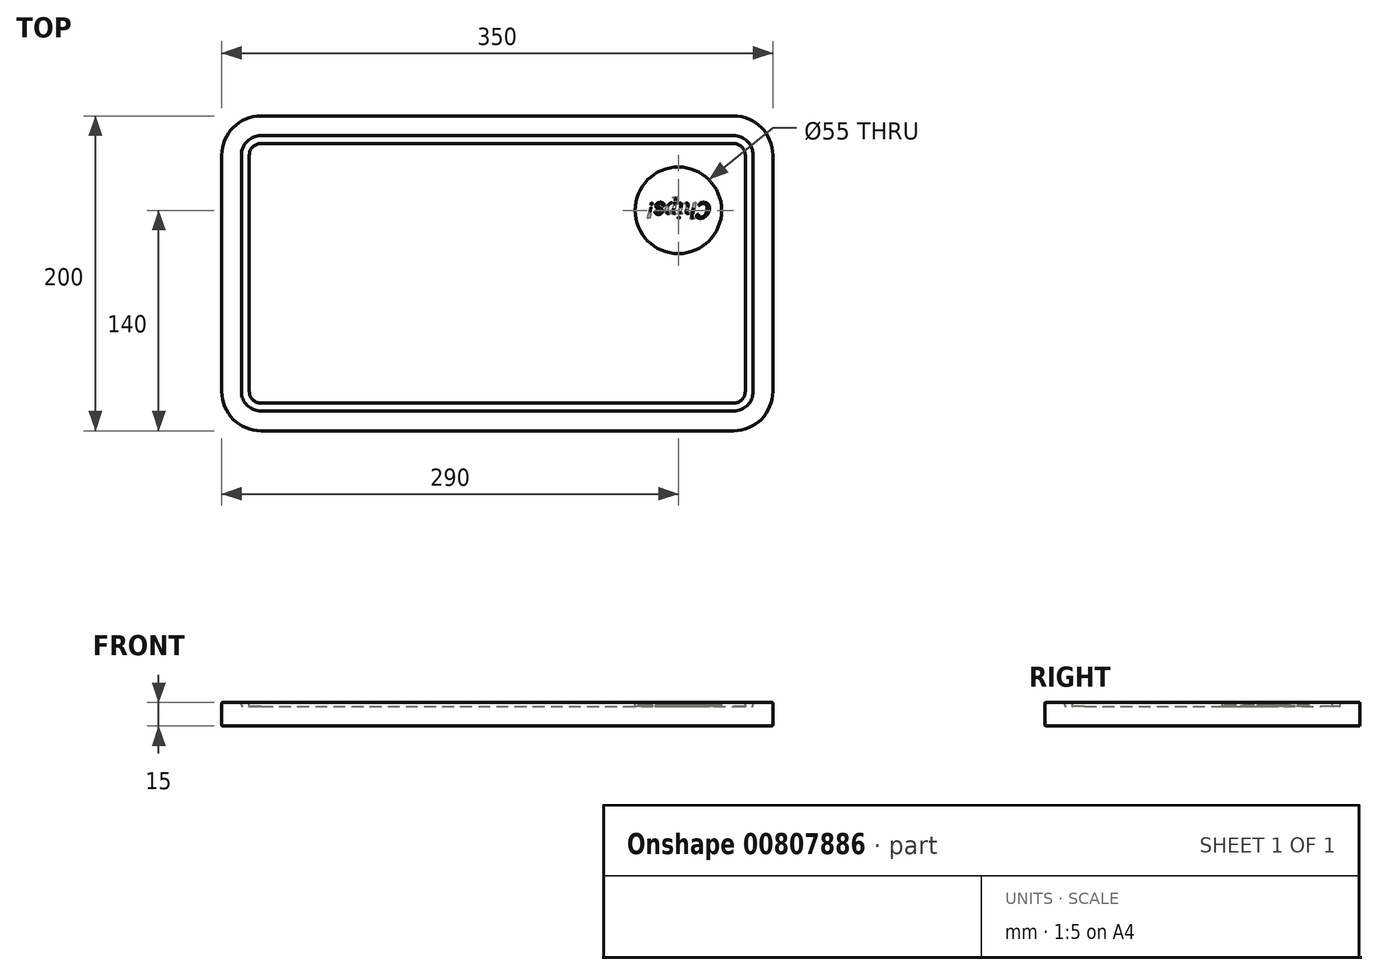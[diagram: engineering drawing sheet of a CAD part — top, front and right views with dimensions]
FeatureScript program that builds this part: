
annotation { "Feature Type Name" : "Feature", "Feature Type Description" : "" }
export const myFeature = defineFeature(function(context is Context, id is Id, definition is map)
    precondition{}
    {
        {
            assignVariable(context, id + "F0", {"name" : "BrdThk", "anyValue" : 15 * mm});
        }
        {
            assignVariable(context, id + "F1", {"name" : "CrnRad", "anyValue" : 25 * mm});
        }
        {
            assignVariable(context, id + "F2", {"name" : "GrvDpth", "anyValue" : 2.5 * mm});
        }
        {
            var Q0;
            Q0=qCreatedBy(makeId("Top.planeOp"),FACE);
            cPlane(context, id + "F3", {"entities" : qUnion([Q0]), "cplaneType" : CPlaneType.OFFSET, "offset" : getVariable(context, 'BrdThk'), "width" : 150 * mm, "height" : 150 * mm});
        }
        {
            var Q0;
            Q0=qCreatedBy(id+"F3.planeOp",FACE);
            cPlane(context, id + "F4", {"entities" : qUnion([Q0]), "cplaneType" : CPlaneType.OFFSET, "offset" : getVariable(context, 'GrvDpth'), "oppositeDirection" : true, "width" : 150 * mm, "height" : 150 * mm});
        }
        {
            var Q0;
            Q0=qCreatedBy(makeId("Top.planeOp"),FACE);
            var sketch = newSketch(context, id + "F5", { "sketchPlane" : qUnion([Q0])});
            skLineSegment(sketch, "E0.bottom", {"start": v(-350, 0) * mm, "end": v(0, 0) * mm});
            skLineSegment(sketch, "E0.top", {"start": v(-350, -200) * mm, "end": v(0, -200) * mm});
            skLineSegment(sketch, "E0.left", {"start": v(-350, 0) * mm, "end": v(-350, -200) * mm});
            skLineSegment(sketch, "E0.right", {"start": v(0, 0) * mm, "end": v(0, -200) * mm});
            skLineSegment(sketch, "E1", {"start": v(-76.31, 0) * mm, "end": v(-267.45, 0) * mm, "construction": true});
            skLineSegment(sketch, "E2", {"start": v(0, 111.25) * mm, "end": v(0, -79.9) * mm, "construction": true});
            skSolve(sketch);
        }
        {
            var Q0;
            Q0=makeQuery(id+"F5.imprint","IMPRINT",FACE,{"disambiguationData":[TD([[makeQuery(id+"F5.imprint","IMPRINT",EDGE,{"derivedFrom":sQuery(id+"F5.wireOp",EDGE,"E0.bottom")}),-1.0]])]});
            var Q1;
            Q1=qCreatedBy(id+"F3.planeOp",FACE);
            extrude(context, id + "F6", {"entities" : qUnion([Q0]), "endBound" : BoundingType.UP_TO_SURFACE, "depth" : 15 * mm, "endBoundEntityFace" : qUnion([Q1]), "offsetDistance" : 25 * mm});
        }
        {
            var Q0;
            Q0=makeQuery(id+"F6.opExtrude","SWEPT_EDGE",EDGE,{"disambiguationData":[OSD([sQuery(id+"F5.wireOp",EDGE,"E0.top"),sQuery(id+"F5.wireOp",EDGE,"E0.left")])]});
            var Q1;
            Q1=makeQuery(id+"F6.opExtrude","SWEPT_EDGE",EDGE,{"disambiguationData":[OSD([sQuery(id+"F5.wireOp",EDGE,"E0.bottom"),sQuery(id+"F5.wireOp",EDGE,"E0.left")])]});
            var Q2;
            Q2=makeQuery(id+"F6.opExtrude","SWEPT_EDGE",EDGE,{"disambiguationData":[OSD([sQuery(id+"F5.wireOp",EDGE,"E0.bottom"),sQuery(id+"F5.wireOp",EDGE,"E0.right")])]});
            var Q3;
            Q3=makeQuery(id+"F6.opExtrude","SWEPT_EDGE",EDGE,{"disambiguationData":[OSD([sQuery(id+"F5.wireOp",EDGE,"E0.top"),sQuery(id+"F5.wireOp",EDGE,"E0.right")])]});
            fillet(context, id + "F7", {"entities" : qUnion([Q0, Q1, Q2, Q3]), "radius" : getVariable(context, 'CrnRad'), "tangentPropagation" : true, "allowEdgeOverflow" : false});
        }
        {
            var Q0;
            Q0=qCreatedBy(id+"F3.planeOp",FACE);
            var sketch = newSketch(context, id + "F8", { "sketchPlane" : qUnion([Q0])});
            skLineSegment(sketch, "E3.0.0", {"start": v(-350, -25) * mm, "end": v(-350, -175) * mm, "construction": true});
            skArc(sketch, "E3.0.1", {"start": v(-350, -175) * mm, "mid": v(-342.68, -192.68) * mm, "end": v(-325, -200) * mm, "construction": true});
            skLineSegment(sketch, "E3.0.2", {"start": v(-325, -200) * mm, "end": v(-25, -200) * mm, "construction": true});
            skArc(sketch, "E3.0.3", {"start": v(-25, -200) * mm, "mid": v(-7.32, -192.68) * mm, "end": v(0, -175) * mm, "construction": true});
            skLineSegment(sketch, "E3.0.4", {"start": v(0, -175) * mm, "end": v(0, -25) * mm, "construction": true});
            skArc(sketch, "E3.0.5", {"start": v(0, -25) * mm, "mid": v(-7.32, -7.32) * mm, "end": v(-25, 0) * mm, "construction": true});
            skLineSegment(sketch, "E3.0.6", {"start": v(-25, 0) * mm, "end": v(-325, 0) * mm, "construction": true});
            skArc(sketch, "E3.0.7", {"start": v(-325, 0) * mm, "mid": v(-342.68, -7.32) * mm, "end": v(-350, -25) * mm, "construction": true});
            skArc(sketch, "E4.0", {"start": v(-325, -12.5) * mm, "mid": v(-333.84, -16.16) * mm, "end": v(-337.5, -25) * mm});
            skLineSegment(sketch, "E4.1", {"start": v(-25, -12.5) * mm, "end": v(-325, -12.5) * mm});
            skLineSegment(sketch, "E4.2", {"start": v(-337.5, -25) * mm, "end": v(-337.5, -175) * mm});
            skArc(sketch, "E4.3", {"start": v(-12.5, -25) * mm, "mid": v(-16.16, -16.16) * mm, "end": v(-25, -12.5) * mm});
            skArc(sketch, "E4.4", {"start": v(-337.5, -175) * mm, "mid": v(-333.84, -183.84) * mm, "end": v(-325, -187.5) * mm});
            skLineSegment(sketch, "E4.5", {"start": v(-325, -187.5) * mm, "end": v(-25, -187.5) * mm});
            skArc(sketch, "E4.6", {"start": v(-25, -187.5) * mm, "mid": v(-16.16, -183.84) * mm, "end": v(-12.5, -175) * mm});
            skLineSegment(sketch, "E4.7", {"start": v(-12.5, -175) * mm, "end": v(-12.5, -25) * mm});
            skArc(sketch, "E5.0", {"start": v(-325, -17.5) * mm, "mid": v(-330.3, -19.7) * mm, "end": v(-332.5, -25) * mm});
            skLineSegment(sketch, "E5.1", {"start": v(-25, -17.5) * mm, "end": v(-325, -17.5) * mm});
            skLineSegment(sketch, "E5.2", {"start": v(-332.5, -25) * mm, "end": v(-332.5, -175) * mm});
            skArc(sketch, "E5.3", {"start": v(-17.5, -25) * mm, "mid": v(-19.7, -19.7) * mm, "end": v(-25, -17.5) * mm});
            skArc(sketch, "E5.4", {"start": v(-332.5, -175) * mm, "mid": v(-330.3, -180.3) * mm, "end": v(-325, -182.5) * mm});
            skLineSegment(sketch, "E5.5", {"start": v(-325, -182.5) * mm, "end": v(-25, -182.5) * mm});
            skArc(sketch, "E5.6", {"start": v(-25, -182.5) * mm, "mid": v(-19.7, -180.3) * mm, "end": v(-17.5, -175) * mm});
            skLineSegment(sketch, "E5.7", {"start": v(-17.5, -175) * mm, "end": v(-17.5, -25) * mm});
            skSolve(sketch);
        }
        {
            var Q0;
            Q0=qCreatedBy(id+"F3.planeOp",FACE);
            var sketch = newSketch(context, id + "F9", { "sketchPlane" : qUnion([Q0])});
            skCircle(sketch, "E6", {"center": v(-60, -60) * mm, "radius": 27.5 * mm});
            skLineSegment(sketch, "E7", {"start": v(-143.32, 0) * mm, "end": v(-334.46, 0) * mm, "construction": true});
            skLineSegment(sketch, "E8", {"start": v(0, 92.79) * mm, "end": v(0, -98.35) * mm, "construction": true});
            skSolve(sketch);
        }
        {
            var Q0;
            Q0 = qSketchRegion(id + "F8", true);
            var Q1;
            Q1 = qSketchRegion(id + "F9", true);
            var Q2;
            Q2=qCreatedBy(id+"F4.planeOp",FACE);
            extrude(context, id + "F10", {"entities" : qUnion([Q0, Q1]), "operationType" : NewBodyOperationType.REMOVE, "endBound" : BoundingType.UP_TO_SURFACE, "oppositeDirection" : true, "depth" : 3 * mm, "endBoundEntityFace" : qUnion([Q2]), "offsetDistance" : 25 * mm});
        }
        {
            var Q0;
            {var subQ0=sQuery(id+"F5.wireOp",EDGE,"E0.right");var subQ1=sQuery(id+"F5.wireOp",EDGE,"E0.top");Q0=makeQuery(id+"F7.opFillet","BLEND_EDGE",EDGE,{"blendedFrom":[makeQuery(id+"F6.opExtrude","SWEPT_EDGE",EDGE,{"disambiguationData":[OSD([subQ1,subQ0])]}),makeQuery(id+"F6.opExtrude","CAP_FACE",FACE,{"disambiguationData":[OSD([sQuery(id+"F5.wireOp",EDGE,"E0.bottom"),subQ1,sQuery(id+"F5.wireOp",EDGE,"E0.left"),subQ0])],"isStart":false})],"blendedInto":[makeQuery(id+"F6.opExtrude","CAP_FACE",FACE,{"disambiguationData":[OSD([sQuery(id+"F5.wireOp",EDGE,"E0.bottom"),subQ1,sQuery(id+"F5.wireOp",EDGE,"E0.left"),subQ0])],"isStart":false})]});}
            var Q1;
            Q1=makeQuery(id+"F6.opExtrude","CAP_EDGE",EDGE,{"disambiguationData":[OSD([sQuery(id+"F5.wireOp",EDGE,"E0.right")])],"isStart":true});
            fillet(context, id + "F11", {"entities" : qUnion([Q0, Q1]), "radius" : .5 * mm, "tangentPropagation" : true, "allowEdgeOverflow" : false});
        }
        {
            var Q0;
            Q0=makeQuery(id+"F10.boolean.opBoolean","COPY",FACE,{"derivedFrom":makeQuery(id+"F10.opExtrude","CAP_FACE",FACE,{"disambiguationData":[OSD([sQuery(id+"F9.wireOp",EDGE,"E6")])],"isStart":false})});
            var Q1;
            Q1=makeQuery(id+"F10.boolean.opBoolean","COPY",FACE,{"derivedFrom":makeQuery(id+"F10.opExtrude","CAP_FACE",FACE,{"disambiguationData":[OSD([sQuery(id+"F8.wireOp",EDGE,"E4.0"),sQuery(id+"F8.wireOp",EDGE,"E4.1"),sQuery(id+"F8.wireOp",EDGE,"E4.2"),sQuery(id+"F8.wireOp",EDGE,"E4.3"),sQuery(id+"F8.wireOp",EDGE,"E4.4"),sQuery(id+"F8.wireOp",EDGE,"E4.5"),sQuery(id+"F8.wireOp",EDGE,"E4.6"),sQuery(id+"F8.wireOp",EDGE,"E4.7"),sQuery(id+"F8.wireOp",EDGE,"E5.0"),sQuery(id+"F8.wireOp",EDGE,"E5.1"),sQuery(id+"F8.wireOp",EDGE,"E5.2"),sQuery(id+"F8.wireOp",EDGE,"E5.3"),sQuery(id+"F8.wireOp",EDGE,"E5.4"),sQuery(id+"F8.wireOp",EDGE,"E5.5"),sQuery(id+"F8.wireOp",EDGE,"E5.6"),sQuery(id+"F8.wireOp",EDGE,"E5.7")])],"isStart":false})});
            fillet(context, id + "F12", {"entities" : qUnion([Q0, Q1]), "radius" : .5 * mm, "tangentPropagation" : true, "allowEdgeOverflow" : false});
        }
        {
            var Q0;
            Q0=qCreatedBy(id+"F4.planeOp",FACE);
            var sketch = newSketch(context, id + "F13", { "sketchPlane" : qUnion([Q0])});
            skCircle(sketch, "E9.0", {"center": v(-60, -60) * mm, "radius": 27.5 * mm});
            skSolve(sketch);
        }
        {
            var Q0;
            Q0 = qSketchRegion(id + "F13", true);
            extrude(context, id + "F14", {"entities" : qUnion([Q0]), "depth" : .5 * mm, "offsetDistance" : 25 * mm});
        }
        {
            var Q0;
            Q0=qCreatedBy(id+"F4.planeOp",FACE);
            var sketch = newSketch(context, id + "F15", { "sketchPlane" : qUnion([Q0])});
            skText(sketch, "E10", { "text": "Chips!", "fontName": "NotoSerif-Italic.ttf"});
            skLineSegment(sketch, "E11", {"start": v(-39.5, -60) * mm, "end": v(-80.5, -60) * mm, "construction": true});
            const initialGuessF15  = {"E10": [-0.0395, -0.055, -1, 0, 0.01]};
            skSetInitialGuess(sketch, initialGuessF15);
            skSolve(sketch);
        }
        {
            var Q0;
            Q0 = qSketchRegion(id + "F15", true);
            extrude(context, id + "F16", {"entities" : qUnion([Q0]), "depth" : .525 * mm, "offsetDistance" : 25 * mm});
        }
        {
            var Q0;
            Q0=makeQuery(id+"F16.opExtrude","CAP_FACE",FACE,{"disambiguationData":[OSD([sQuery(id+"F15.wireOp",EDGE,"E10.sketch_text.stroke-0"),sQuery(id+"F15.wireOp",EDGE,"E10.sketch_text.stroke-1"),sQuery(id+"F15.wireOp",EDGE,"E10.sketch_text.stroke-2"),sQuery(id+"F15.wireOp",EDGE,"E10.sketch_text.stroke-3"),sQuery(id+"F15.wireOp",EDGE,"E10.sketch_text.stroke-4"),sQuery(id+"F15.wireOp",EDGE,"E10.sketch_text.stroke-5"),sQuery(id+"F15.wireOp",EDGE,"E10.sketch_text.stroke-6"),sQuery(id+"F15.wireOp",EDGE,"E10.sketch_text.stroke-7"),sQuery(id+"F15.wireOp",EDGE,"E10.sketch_text.stroke-8"),sQuery(id+"F15.wireOp",EDGE,"E10.sketch_text.stroke-9"),sQuery(id+"F15.wireOp",EDGE,"E10.sketch_text.stroke-10"),sQuery(id+"F15.wireOp",EDGE,"E10.sketch_text.stroke-11"),sQuery(id+"F15.wireOp",EDGE,"E10.sketch_text.stroke-12"),sQuery(id+"F15.wireOp",EDGE,"E10.sketch_text.stroke-13"),sQuery(id+"F15.wireOp",EDGE,"E10.sketch_text.stroke-14"),sQuery(id+"F15.wireOp",EDGE,"E10.sketch_text.stroke-15")])],"isStart":false});
            var Q1;
            Q1=makeQuery(id+"F16.opExtrude","CAP_FACE",FACE,{"disambiguationData":[OSD([sQuery(id+"F15.wireOp",EDGE,"E10.sketch_text.stroke-16"),sQuery(id+"F15.wireOp",EDGE,"E10.sketch_text.stroke-17"),sQuery(id+"F15.wireOp",EDGE,"E10.sketch_text.stroke-18"),sQuery(id+"F15.wireOp",EDGE,"E10.sketch_text.stroke-19"),sQuery(id+"F15.wireOp",EDGE,"E10.sketch_text.stroke-20"),sQuery(id+"F15.wireOp",EDGE,"E10.sketch_text.stroke-21"),sQuery(id+"F15.wireOp",EDGE,"E10.sketch_text.stroke-22"),sQuery(id+"F15.wireOp",EDGE,"E10.sketch_text.stroke-23"),sQuery(id+"F15.wireOp",EDGE,"E10.sketch_text.stroke-24"),sQuery(id+"F15.wireOp",EDGE,"E10.sketch_text.stroke-25"),sQuery(id+"F15.wireOp",EDGE,"E10.sketch_text.stroke-26"),sQuery(id+"F15.wireOp",EDGE,"E10.sketch_text.stroke-27"),sQuery(id+"F15.wireOp",EDGE,"E10.sketch_text.stroke-28"),sQuery(id+"F15.wireOp",EDGE,"E10.sketch_text.stroke-29"),sQuery(id+"F15.wireOp",EDGE,"E10.sketch_text.stroke-30"),sQuery(id+"F15.wireOp",EDGE,"E10.sketch_text.stroke-31"),sQuery(id+"F15.wireOp",EDGE,"E10.sketch_text.stroke-32"),sQuery(id+"F15.wireOp",EDGE,"E10.sketch_text.stroke-33"),sQuery(id+"F15.wireOp",EDGE,"E10.sketch_text.stroke-34"),sQuery(id+"F15.wireOp",EDGE,"E10.sketch_text.stroke-35"),sQuery(id+"F15.wireOp",EDGE,"E10.sketch_text.stroke-36"),sQuery(id+"F15.wireOp",EDGE,"E10.sketch_text.stroke-37"),sQuery(id+"F15.wireOp",EDGE,"E10.sketch_text.stroke-38"),sQuery(id+"F15.wireOp",EDGE,"E10.sketch_text.stroke-39"),sQuery(id+"F15.wireOp",EDGE,"E10.sketch_text.stroke-40"),sQuery(id+"F15.wireOp",EDGE,"E10.sketch_text.stroke-41"),sQuery(id+"F15.wireOp",EDGE,"E10.sketch_text.stroke-42"),sQuery(id+"F15.wireOp",EDGE,"E10.sketch_text.stroke-43")])],"isStart":false});
            var Q2;
            Q2=makeQuery(id+"F16.opExtrude","CAP_FACE",FACE,{"disambiguationData":[OSD([sQuery(id+"F15.wireOp",EDGE,"E10.sketch_text.stroke-50"),sQuery(id+"F15.wireOp",EDGE,"E10.sketch_text.stroke-51"),sQuery(id+"F15.wireOp",EDGE,"E10.sketch_text.stroke-52"),sQuery(id+"F15.wireOp",EDGE,"E10.sketch_text.stroke-53"),sQuery(id+"F15.wireOp",EDGE,"E10.sketch_text.stroke-54"),sQuery(id+"F15.wireOp",EDGE,"E10.sketch_text.stroke-55"),sQuery(id+"F15.wireOp",EDGE,"E10.sketch_text.stroke-56"),sQuery(id+"F15.wireOp",EDGE,"E10.sketch_text.stroke-57"),sQuery(id+"F15.wireOp",EDGE,"E10.sketch_text.stroke-58"),sQuery(id+"F15.wireOp",EDGE,"E10.sketch_text.stroke-59"),sQuery(id+"F15.wireOp",EDGE,"E10.sketch_text.stroke-60"),sQuery(id+"F15.wireOp",EDGE,"E10.sketch_text.stroke-61"),sQuery(id+"F15.wireOp",EDGE,"E10.sketch_text.stroke-62"),sQuery(id+"F15.wireOp",EDGE,"E10.sketch_text.stroke-63"),sQuery(id+"F15.wireOp",EDGE,"E10.sketch_text.stroke-64")])],"isStart":false});
            var Q3;
            Q3=makeQuery(id+"F16.opExtrude","CAP_FACE",FACE,{"disambiguationData":[OSD([sQuery(id+"F15.wireOp",EDGE,"E10.sketch_text.stroke-44"),sQuery(id+"F15.wireOp",EDGE,"E10.sketch_text.stroke-45"),sQuery(id+"F15.wireOp",EDGE,"E10.sketch_text.stroke-46"),sQuery(id+"F15.wireOp",EDGE,"E10.sketch_text.stroke-47"),sQuery(id+"F15.wireOp",EDGE,"E10.sketch_text.stroke-48"),sQuery(id+"F15.wireOp",EDGE,"E10.sketch_text.stroke-49")])],"isStart":false});
            var Q4;
            Q4=makeQuery(id+"F16.opExtrude","CAP_FACE",FACE,{"disambiguationData":[OSD([sQuery(id+"F15.wireOp",EDGE,"E10.sketch_text.stroke-65"),sQuery(id+"F15.wireOp",EDGE,"E10.sketch_text.stroke-66"),sQuery(id+"F15.wireOp",EDGE,"E10.sketch_text.stroke-67"),sQuery(id+"F15.wireOp",EDGE,"E10.sketch_text.stroke-68"),sQuery(id+"F15.wireOp",EDGE,"E10.sketch_text.stroke-69"),sQuery(id+"F15.wireOp",EDGE,"E10.sketch_text.stroke-70"),sQuery(id+"F15.wireOp",EDGE,"E10.sketch_text.stroke-71"),sQuery(id+"F15.wireOp",EDGE,"E10.sketch_text.stroke-72"),sQuery(id+"F15.wireOp",EDGE,"E10.sketch_text.stroke-73"),sQuery(id+"F15.wireOp",EDGE,"E10.sketch_text.stroke-74"),sQuery(id+"F15.wireOp",EDGE,"E10.sketch_text.stroke-75"),sQuery(id+"F15.wireOp",EDGE,"E10.sketch_text.stroke-76"),sQuery(id+"F15.wireOp",EDGE,"E10.sketch_text.stroke-77"),sQuery(id+"F15.wireOp",EDGE,"E10.sketch_text.stroke-78"),sQuery(id+"F15.wireOp",EDGE,"E10.sketch_text.stroke-79"),sQuery(id+"F15.wireOp",EDGE,"E10.sketch_text.stroke-80"),sQuery(id+"F15.wireOp",EDGE,"E10.sketch_text.stroke-81"),sQuery(id+"F15.wireOp",EDGE,"E10.sketch_text.stroke-82"),sQuery(id+"F15.wireOp",EDGE,"E10.sketch_text.stroke-83"),sQuery(id+"F15.wireOp",EDGE,"E10.sketch_text.stroke-84"),sQuery(id+"F15.wireOp",EDGE,"E10.sketch_text.stroke-85"),sQuery(id+"F15.wireOp",EDGE,"E10.sketch_text.stroke-86"),sQuery(id+"F15.wireOp",EDGE,"E10.sketch_text.stroke-87"),sQuery(id+"F15.wireOp",EDGE,"E10.sketch_text.stroke-88"),sQuery(id+"F15.wireOp",EDGE,"E10.sketch_text.stroke-89"),sQuery(id+"F15.wireOp",EDGE,"E10.sketch_text.stroke-90"),sQuery(id+"F15.wireOp",EDGE,"E10.sketch_text.stroke-91"),sQuery(id+"F15.wireOp",EDGE,"E10.sketch_text.stroke-92")])],"isStart":false});
            var Q5;
            Q5=makeQuery(id+"F16.opExtrude","CAP_FACE",FACE,{"disambiguationData":[OSD([sQuery(id+"F15.wireOp",EDGE,"E10.sketch_text.stroke-93"),sQuery(id+"F15.wireOp",EDGE,"E10.sketch_text.stroke-94"),sQuery(id+"F15.wireOp",EDGE,"E10.sketch_text.stroke-95"),sQuery(id+"F15.wireOp",EDGE,"E10.sketch_text.stroke-96"),sQuery(id+"F15.wireOp",EDGE,"E10.sketch_text.stroke-97"),sQuery(id+"F15.wireOp",EDGE,"E10.sketch_text.stroke-98"),sQuery(id+"F15.wireOp",EDGE,"E10.sketch_text.stroke-99"),sQuery(id+"F15.wireOp",EDGE,"E10.sketch_text.stroke-100"),sQuery(id+"F15.wireOp",EDGE,"E10.sketch_text.stroke-101"),sQuery(id+"F15.wireOp",EDGE,"E10.sketch_text.stroke-102"),sQuery(id+"F15.wireOp",EDGE,"E10.sketch_text.stroke-103"),sQuery(id+"F15.wireOp",EDGE,"E10.sketch_text.stroke-104"),sQuery(id+"F15.wireOp",EDGE,"E10.sketch_text.stroke-105"),sQuery(id+"F15.wireOp",EDGE,"E10.sketch_text.stroke-106"),sQuery(id+"F15.wireOp",EDGE,"E10.sketch_text.stroke-107"),sQuery(id+"F15.wireOp",EDGE,"E10.sketch_text.stroke-108"),sQuery(id+"F15.wireOp",EDGE,"E10.sketch_text.stroke-109"),sQuery(id+"F15.wireOp",EDGE,"E10.sketch_text.stroke-110"),sQuery(id+"F15.wireOp",EDGE,"E10.sketch_text.stroke-111"),sQuery(id+"F15.wireOp",EDGE,"E10.sketch_text.stroke-112"),sQuery(id+"F15.wireOp",EDGE,"E10.sketch_text.stroke-113"),sQuery(id+"F15.wireOp",EDGE,"E10.sketch_text.stroke-114"),sQuery(id+"F15.wireOp",EDGE,"E10.sketch_text.stroke-115"),sQuery(id+"F15.wireOp",EDGE,"E10.sketch_text.stroke-116"),sQuery(id+"F15.wireOp",EDGE,"E10.sketch_text.stroke-117")])],"isStart":false});
            var Q6;
            Q6=makeQuery(id+"F16.opExtrude","CAP_FACE",FACE,{"disambiguationData":[OSD([sQuery(id+"F15.wireOp",EDGE,"E10.sketch_text.stroke-118"),sQuery(id+"F15.wireOp",EDGE,"E10.sketch_text.stroke-119"),sQuery(id+"F15.wireOp",EDGE,"E10.sketch_text.stroke-120"),sQuery(id+"F15.wireOp",EDGE,"E10.sketch_text.stroke-121")])],"isStart":false});
            var Q7;
            Q7=makeQuery(id+"F16.opExtrude","CAP_FACE",FACE,{"disambiguationData":[OSD([sQuery(id+"F15.wireOp",EDGE,"E10.sketch_text.stroke-122"),sQuery(id+"F15.wireOp",EDGE,"E10.sketch_text.stroke-123"),sQuery(id+"F15.wireOp",EDGE,"E10.sketch_text.stroke-124"),sQuery(id+"F15.wireOp",EDGE,"E10.sketch_text.stroke-125"),sQuery(id+"F15.wireOp",EDGE,"E10.sketch_text.stroke-126"),sQuery(id+"F15.wireOp",EDGE,"E10.sketch_text.stroke-127")])],"isStart":false});
            fillet(context, id + "F17", {"entities" : qUnion([Q0, Q1, Q2, Q3, Q4, Q5, Q6, Q7]), "radius" : .5 * mm, "tangentPropagation" : true, "allowEdgeOverflow" : false});
        }
    });
